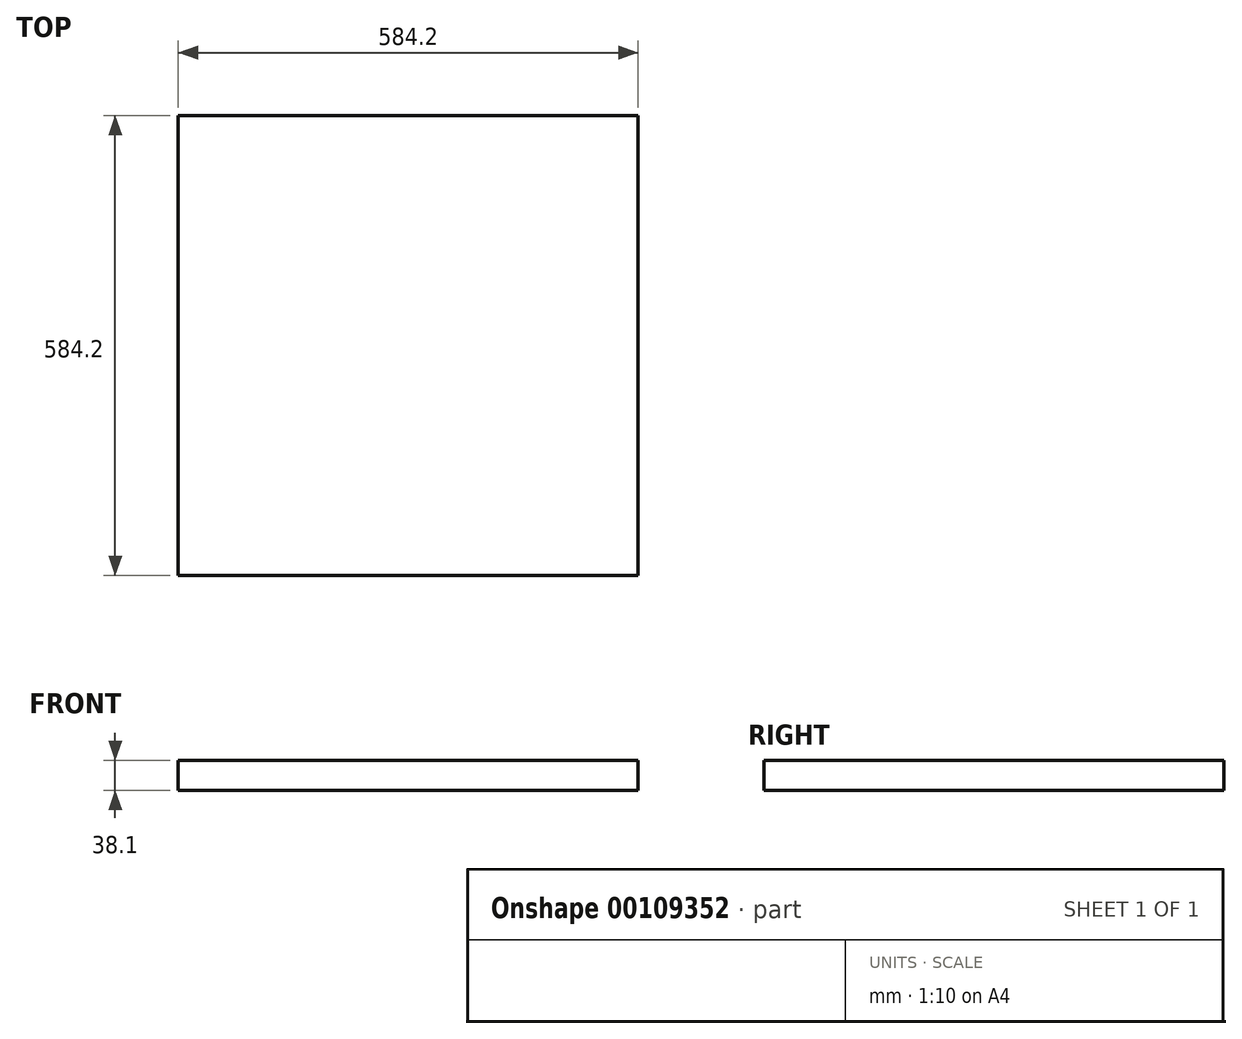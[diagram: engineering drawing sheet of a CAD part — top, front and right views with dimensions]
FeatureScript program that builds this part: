
annotation { "Feature Type Name" : "Feature", "Feature Type Description" : "" }
export const myFeature = defineFeature(function(context is Context, id is Id, definition is map)
    precondition{}
    {
        {
            var Q0;
            Q0=qCreatedBy(makeId("Top.planeOp"),FACE);
            var sketch = newSketch(context, id + "F0", { "sketchPlane" : qUnion([Q0])});
            skLineSegment(sketch, "E0.bottom", {"start": v(0, 0) * mm, "end": v(584.2, 0) * mm});
            skLineSegment(sketch, "E0.top", {"start": v(0, 584.2) * mm, "end": v(584.2, 584.2) * mm});
            skLineSegment(sketch, "E0.left", {"start": v(0, 0) * mm, "end": v(0, 584.2) * mm});
            skLineSegment(sketch, "E0.right", {"start": v(584.2, 0) * mm, "end": v(584.2, 584.2) * mm});
            skSolve(sketch);
        }
        {
            var Q0;
            Q0=makeQuery(id+"F0.imprint","IMPRINT",FACE,{"disambiguationData":[TD([[makeQuery(id+"F0.imprint","IMPRINT",EDGE,{"derivedFrom":sQuery(id+"F0.wireOp",EDGE,"E0.bottom")}),1.0]])]});
            extrude(context, id + "F1", {"entities" : qUnion([Q0]), "depth" : 38.1 * mm});
        }
    });
